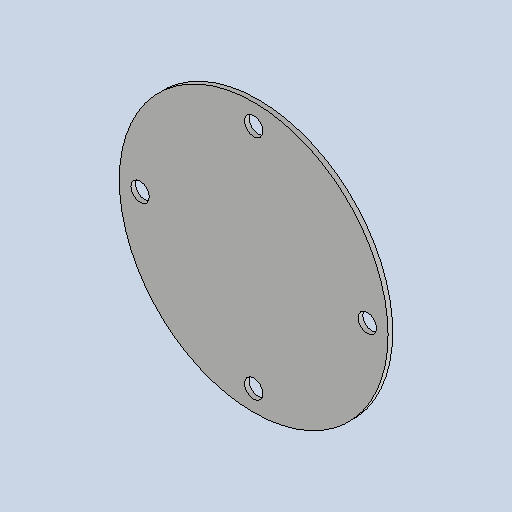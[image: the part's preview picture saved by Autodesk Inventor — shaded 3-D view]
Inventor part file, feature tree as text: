
AUTODESK INVENTOR PART (.ipt)
format: ipt  version: 2025 (Build 290162010, 162A)  size: 108,544 bytes
history: native  units: mm
features: sketch x2, sheet_metal_op x1, extrude x1, pattern_circular x1, other x1
ambient origin geometry x8: Origin, YZ Plane, XZ Plane, XY Plane, X Axis, Y Axis, Z Axis, Center Point
bodies: Solid1 (feature_tree)
feature tree (6):
  sheet_metal_op  "Face1"
  extrude  "Extrusion1"  Depth=3.0mm
  pattern_circular  "Circular Pattern1"  Count=8  [1 undecoded]
  sketch  "Sketch1"  dims[d0=175.0mm d1=3.0mm d2=80.0mm]
  other  "Plate1"
  sketch  "Sketch2"  dims[d3=80.0mm d8=0.0mm d9=0.0mm d10=40.0mm d11=360.0deg d16=12.0mm d17=13.5mm d18=0.5mm d19=0.872665mm d20=0.5mm d21=0.872665mm]
note: 1 required parameter value undecoded (feature->parameter linkage not recoverable at this tier; creation-order binding heuristic only, values carry confidence <= 0.55)
